# Revit family: NBS_Allermuir_DmstcChrs_Jinx_JNX03
name_source: partatom
category: Furniture
revit_build: Autodesk Revit 2016 (Build: 20161004_0715(x64)
units: mm (PartAtom-declared; Revit-internal decimal feet)

## family parameters
Always vertical = Yes
Cut with Voids When Loaded = No
Room Calculation Point = No
Shared = No
Work Plane-Based = No

## types (1)
- JNX03
    AssetType = Moveable
    BIMObjectName = NBS_Allermuir_DomesticChairs_Jinx_JNX03
    Category = Pr_40_50_12_22:Dining chairs
    Description = 3 seat sofa
    DurationUnit = year
    EnvironmentalProductDeclaration = http://www.thesenatorgroup.com
    ExpectedLife = 5
    Features = Wood carcass construction, dual desinsity back foam, sprung seat foam, fully upholstered, platic glides, plastic glides with felt, two tone upholstery
    FramesMaterial = Wood
    HighestSeatingHeight = 0 mm  [stored 0 ft]
    IfcExportAs = IfcFurnitureType
    IfcExportType = SOFA
    IsBuiltIn = No
    LowestSeatingHeight = 0 mm  [stored 0 ft]
    ManufacturerName = Allermuir
    ManufacturerURL = http://www.thesenatorgroup.com
    ModelNumber = JNX03
    ModelReference = Jinx
    NBSCertification = www.nationalbimlibrary.com/cert/bguxwvwj
    NBSDescription = Domestic chairs
    NBSReference = 45-35-20/365
    Name = DomesticChairs_Jinx_JNX03_Allermuir
    NominalDepth = 2540 mm
    NominalHeight = 665 mm
    NominalLength = 965 mm
    NominalWidth = 2540 mm
    ProductInformation = http://www.thesenatorgroup.com
    SeatingHeight = 410 mm
    SeatingSeatMaterial = NBS_Concept
    SeatsAndBacksMaterial = Upholstered
    ShelfMaterial = NBS_Concept
    Size = 965 x 2540 x 965 mm
    Status = UNSET
    Uniclass2015Code = Pr_40_50_12_22
    Uniclass2015Title = Dining chairs
    Uniclass2015Version = Products v1.9
    Version = 1
    WarrantyDescription = Allermuir warrant that its manufactured products are free from manufacturing defects in materials or workmanship for a period of five years
    WarrantyDurationParts = 5
    WarrantyDurationUnit = year

note: [stored X ft] marks values corroborated as IEEE doubles in the binary element streams (Revit-internal decimal feet)

## geometry (parser evidence)
native form markers: Sweep x3
no freeform markers — native parametric forms only
